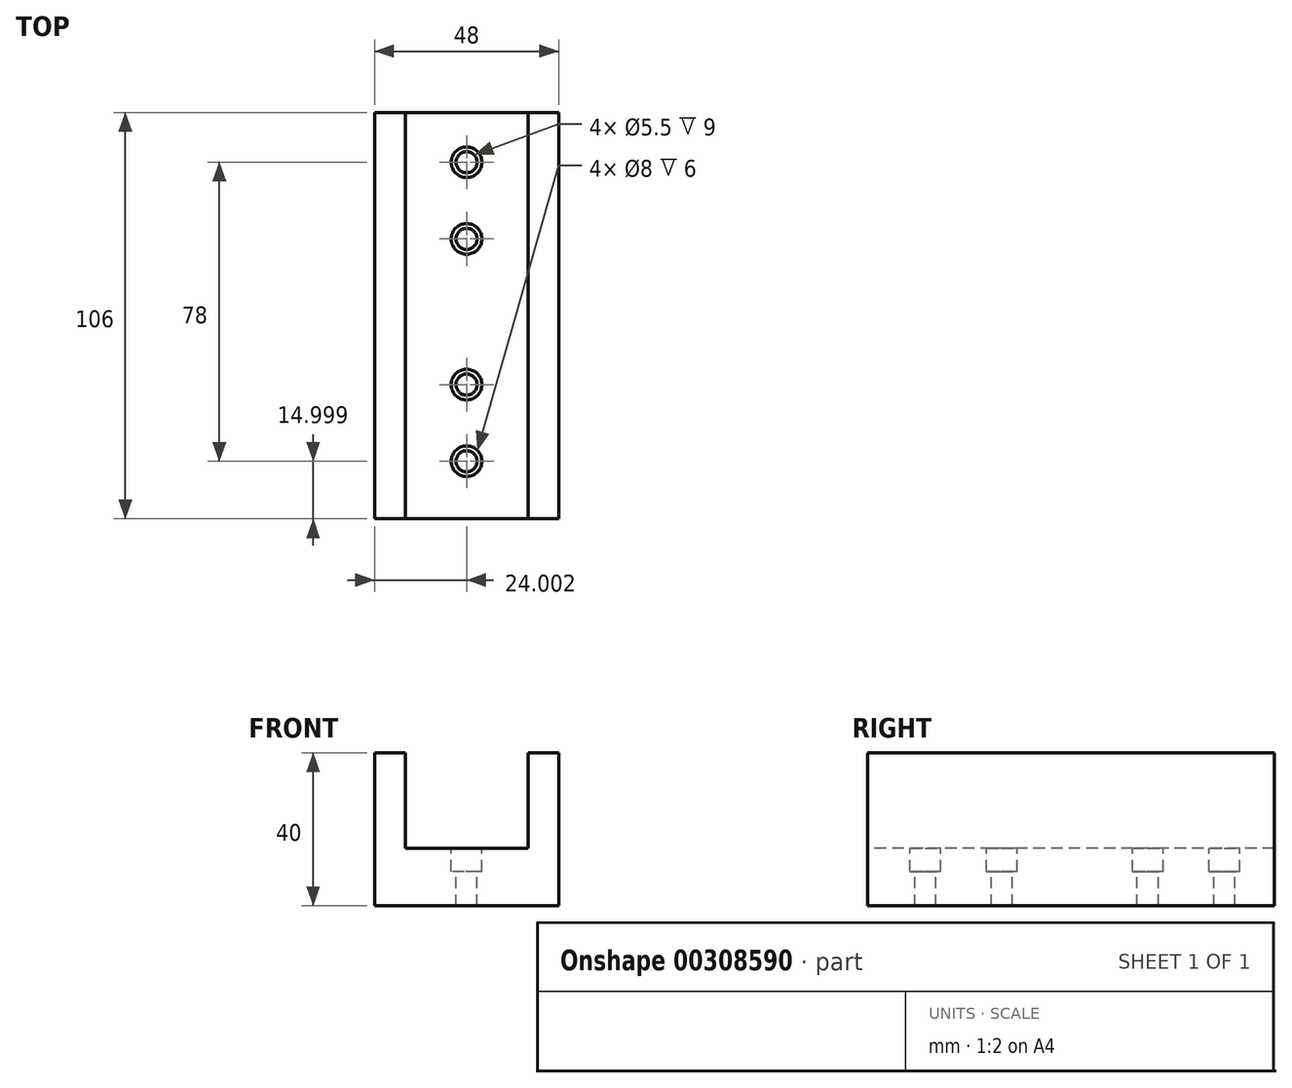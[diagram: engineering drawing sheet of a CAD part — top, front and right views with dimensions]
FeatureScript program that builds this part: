
annotation { "Feature Type Name" : "Feature", "Feature Type Description" : "" }
export const myFeature = defineFeature(function(context is Context, id is Id, definition is map)
    precondition{}
    {
        {
            var Q0;
            Q0=qCreatedBy(makeId("Top.planeOp"),FACE);
            var sketch = newSketch(context, id + "F0", { "sketchPlane" : qUnion([Q0])});
            skLineSegment(sketch, "E0.bottom", {"start": v(-14.28, 73.83) * mm, "end": v(33.72, 73.83) * mm});
            skLineSegment(sketch, "E0.top", {"start": v(-14.28, -32.17) * mm, "end": v(33.72, -32.17) * mm});
            skLineSegment(sketch, "E0.left", {"start": v(-14.28, 73.83) * mm, "end": v(-14.28, -32.17) * mm});
            skLineSegment(sketch, "E0.right", {"start": v(33.72, 73.83) * mm, "end": v(33.72, -32.17) * mm});
            skSolve(sketch);
        }
        {
            var Q0;
            Q0=makeQuery(id+"F0.imprint","IMPRINT",FACE,{"disambiguationData":[TD([[makeQuery(id+"F0.imprint","IMPRINT",EDGE,{"derivedFrom":sQuery(id+"F0.wireOp",EDGE,"E0.bottom")}),-1.0]])]});
            extrude(context, id + "F1", {"entities" : qUnion([Q0]), "endBound" : BoundingType.SYMMETRIC, "depth" : 15 * mm});
        }
        {
            var Q0;
            Q0=makeQuery(id+"F1.opExtrude","CAP_FACE",FACE,{"disambiguationData":[OSD([sQuery(id+"F0.wireOp",EDGE,"E0.bottom"),sQuery(id+"F0.wireOp",EDGE,"E0.top"),sQuery(id+"F0.wireOp",EDGE,"E0.left"),sQuery(id+"F0.wireOp",EDGE,"E0.right")])],"isStart":true});
            var sketch = newSketch(context, id + "F2", { "sketchPlane" : qUnion([Q0])});
            skLineSegment(sketch, "E1", {"start": v(9.72, 32.17) * mm, "end": v(9.72, -73.83) * mm, "construction": true});
            skLineSegment(sketch, "E2", {"start": v(33.72, -20.83) * mm, "end": v(-14.28, -20.83) * mm, "construction": true});
            skLineSegment(sketch, "E3.bottom", {"start": v(24.72, 9.17) * mm, "end": v(-5.28, 9.17) * mm});
            skLineSegment(sketch, "E3.top", {"start": v(24.72, -50.83) * mm, "end": v(-5.28, -50.83) * mm});
            skLineSegment(sketch, "E3.left", {"start": v(24.72, 9.17) * mm, "end": v(24.72, -50.83) * mm});
            skLineSegment(sketch, "E3.right", {"start": v(-5.28, 9.17) * mm, "end": v(-5.28, -50.83) * mm});
            skPoint(sketch, "E3.middle", {"position": v(9.72, -20.83) * mm});
            skSolve(sketch);
        }
        {
            var Q0;
            Q0=makeQuery(id+"F1.opExtrude","CAP_FACE",FACE,{"disambiguationData":[OSD([sQuery(id+"F0.wireOp",EDGE,"E0.bottom"),sQuery(id+"F0.wireOp",EDGE,"E0.top"),sQuery(id+"F0.wireOp",EDGE,"E0.left"),sQuery(id+"F0.wireOp",EDGE,"E0.right")])],"isStart":false});
            var sketch = newSketch(context, id + "F3", { "sketchPlane" : qUnion([Q0])});
            skLineSegment(sketch, "E4", {"start": v(-6.28, 73.83) * mm, "end": v(-6.28, 20.83) * mm});
            skLineSegment(sketch, "E5", {"start": v(25.72, 73.83) * mm, "end": v(25.72, 20.83) * mm});
            skLineSegment(sketch, "E6", {"start": v(-14.28, 20.83) * mm, "end": v(33.72, 20.83) * mm, "construction": true});
            skLineSegment(sketch, "E7", {"start": v(33.72, 50.22) * mm, "end": v(-14.28, 50.22) * mm, "construction": true});
            skLineSegment(sketch, "E8", {"start": v(-14.28, -10.35) * mm, "end": v(33.72, -10.35) * mm, "construction": true});
            skPoint(sketch, "E9.trimOffspring.end.orphan", {"position": v(-6.28, -32.17) * mm});
            skPoint(sketch, "E10.orphan", {"position": v(25.72, -32.17) * mm});
            skLineSegment(sketch, "E11", {"start": v(-6.28, 20.83) * mm, "end": v(-6.28, -32.17) * mm});
            skLineSegment(sketch, "E12", {"start": v(25.72, 20.83) * mm, "end": v(25.72, -32.17) * mm});
            skLineSegment(sketch, "E13", {"start": v(-14.28, -32.17) * mm, "end": v(-6.28, -32.17) * mm});
            skLineSegment(sketch, "E14", {"start": v(25.72, -32.17) * mm, "end": v(33.72, -32.17) * mm});
            skSolve(sketch);
        }
        {
            var Q0;
            {var subQ0=sQuery(id+"F3.wireOp",EDGE,"E4");Q0=makeQuery(id+"F3.imprint","IMPRINT",FACE,{"disambiguationData":[TD([[makeQuery(id+"F3.imprint","IMPRINT",EDGE,{"derivedFrom":subQ0}),-1.0]])]});}
            var Q1;
            {var subQ0=sQuery(id+"F3.wireOp",EDGE,"E5");Q1=makeQuery(id+"F3.imprint","IMPRINT",FACE,{"disambiguationData":[TD([[makeQuery(id+"F3.imprint","IMPRINT",EDGE,{"derivedFrom":subQ0}),1.0]])]});}
            extrude(context, id + "F4", {"entities" : qUnion([Q0, Q1]), "operationType" : NewBodyOperationType.ADD, "depth" : 25 * mm});
        }
        {
            var Q0;
            Q0=makeQuery(id+"F1.opExtrude","CAP_FACE",FACE,{"disambiguationData":[OSD([sQuery(id+"F0.wireOp",EDGE,"E0.bottom"),sQuery(id+"F0.wireOp",EDGE,"E0.top"),sQuery(id+"F0.wireOp",EDGE,"E0.left"),sQuery(id+"F0.wireOp",EDGE,"E0.right")])],"isStart":false});
            var sketch = newSketch(context, id + "F5", { "sketchPlane" : qUnion([Q0])});
            skLineSegment(sketch, "E15", {"start": v(9.72, -32.17) * mm, "end": v(9.72, 73.83) * mm, "construction": true});
            skPoint(sketch, "E16", {"position": v(9.72, 40.83) * mm});
            skPoint(sketch, "E17", {"position": v(9.72, 60.83) * mm});
            skPoint(sketch, "E18", {"position": v(9.72, -17.17) * mm});
            skPoint(sketch, "E19", {"position": v(9.72, 2.83) * mm});
            skSolve(sketch);
        }
        {
            var Q0;
            Q0=sQuery(id+"F5.wireOp",VERTEX,"E16");
            var Q1;
            Q1=sQuery(id+"F5.wireOp",VERTEX,"E17");
            var Q2;
            Q2=sQuery(id+"F5.wireOp",VERTEX,"E19");
            var Q3;
            Q3=sQuery(id+"F5.wireOp",VERTEX,"E18");
            var Q4;
            Q4=makeQuery(id+"F1.opExtrude","SWEPT_BODY",BODY,{"disambiguationData":[OSD([sQuery(id+"F0.wireOp",EDGE,"E0.bottom"),sQuery(id+"F0.wireOp",EDGE,"E0.top"),sQuery(id+"F0.wireOp",EDGE,"E0.left"),sQuery(id+"F0.wireOp",EDGE,"E0.right")])]});
            hole(context, id + "F6", {"style" : HoleStyle.C_BORE, "endStyle" : HoleEndStyle.THROUGH, "holeDiameter" : 5.5 * mm, "cBoreDiameter" : 8 * mm, "cBoreDepth" : 6 * mm, "tappedDepth" : 12 * mm, "tapClearance" : 3, "locations" : qUnion([Q0, Q1, Q2, Q3]), "scope" : qUnion([Q4])});
        }
    });
